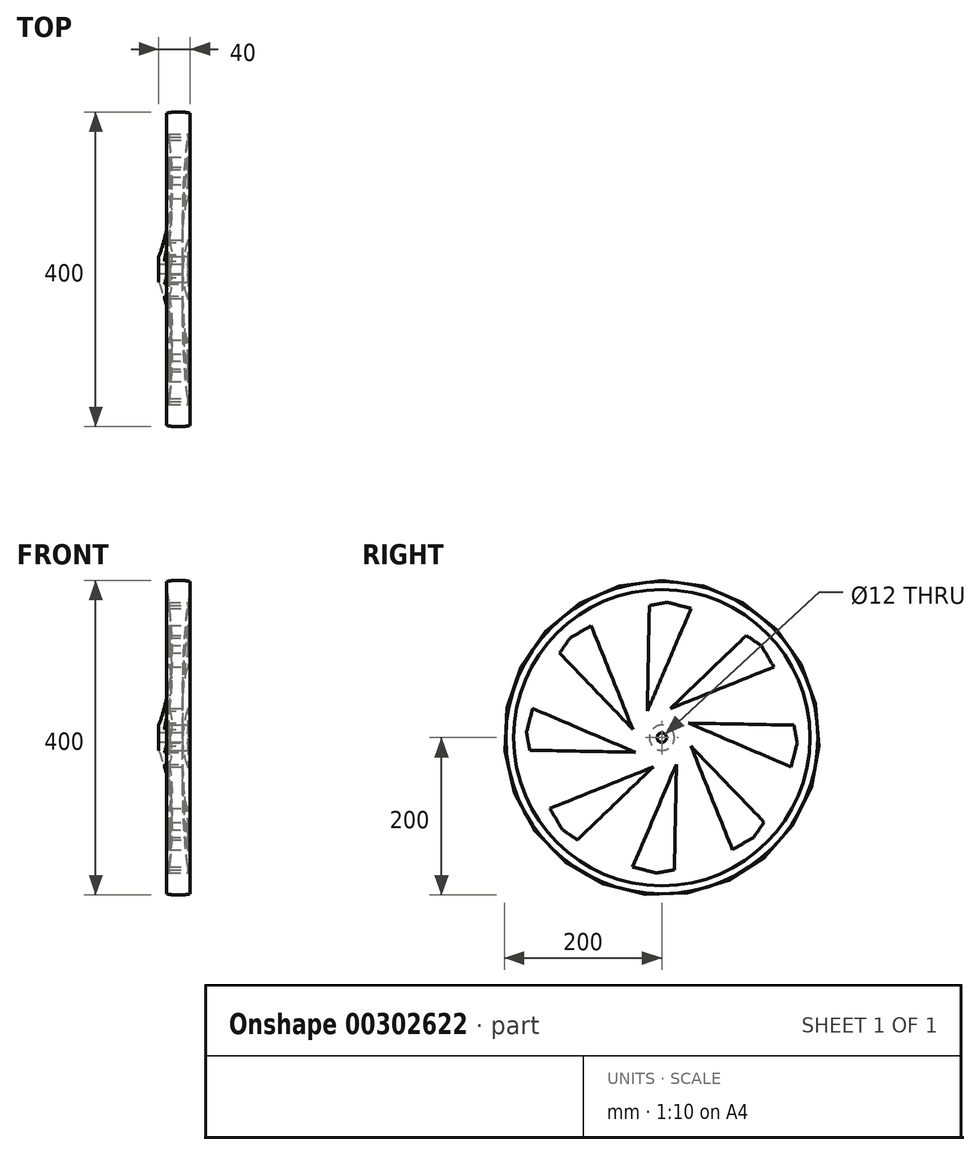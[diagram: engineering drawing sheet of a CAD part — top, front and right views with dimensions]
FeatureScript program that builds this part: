
annotation { "Feature Type Name" : "Feature", "Feature Type Description" : "" }
export const myFeature = defineFeature(function(context is Context, id is Id, definition is map)
    precondition{}
    {
        {
            var Q0;
            Q0=qCreatedBy(makeId("Front.planeOp"),FACE);
            var sketch = newSketch(context, id + "F0", { "sketchPlane" : qUnion([Q0])});
            skLineSegment(sketch, "E0", {"start": v(0, 0) * mm, "end": v(55.9, 0) * mm});
            skLineSegment(sketch, "E1", {"start": v(0, 0) * mm, "end": v(0, 200) * mm});
            skArc(sketch, "E2", {"start": v(15, 198.25) * mm, "mid": v(0, 200) * mm, "end": v(-15, 198.25) * mm});
            skLineSegment(sketch, "E3", {"start": v(-15, 198.25) * mm, "end": v(15, 198.25) * mm});
            skLineSegment(sketch, "E4", {"start": v(0, 0) * mm, "end": v(0, 6) * mm});
            skLineSegment(sketch, "E5", {"start": v(0, 6) * mm, "end": v(5, 6) * mm});
            skLineSegment(sketch, "E6", {"start": v(0, 6) * mm, "end": v(-25, 6) * mm});
            skLineSegment(sketch, "E7.top", {"start": v(-15, 188.25) * mm, "end": v(15, 188.25) * mm});
            skLineSegment(sketch, "E7.left", {"start": v(-15, 198.25) * mm, "end": v(-15, 188.25) * mm});
            skLineSegment(sketch, "E7.right", {"start": v(15, 198.25) * mm, "end": v(15, 188.25) * mm});
            skLineSegment(sketch, "E8.bottom", {"start": v(-25, 6) * mm, "end": v(5, 6) * mm});
            skLineSegment(sketch, "E8.top", {"start": v(-25, 16) * mm, "end": v(5, 16) * mm});
            skLineSegment(sketch, "E8.left", {"start": v(-25, 6) * mm, "end": v(-25, 16) * mm});
            skLineSegment(sketch, "E8.right", {"start": v(5, 6) * mm, "end": v(5, 16) * mm});
            skFitSpline(sketch, "E9", {"points": [v(15, 188.25) * mm, v(5, 16) * mm], "startDerivative": vector(-30, -169.88) * mm, "endDerivative": vector(0, -171.97) * mm});
            skFitSpline(sketch, "E10", {"points": [v(-15, 188.25) * mm, v(-25, 16) * mm], "startDerivative": vector(30, -169.88) * mm, "endDerivative": vector(-60, -162.6) * mm});
            skSolve(sketch);
        }
        {
            var Q0;
            Q0 = qSketchRegion(id + "F0", true);
            var Q1;
            Q1=sQuery(id+"F0.wireOp",EDGE,"E0");
            revolve(context, id + "F1", {"entities" : qUnion([Q0]), "axis" : qUnion([Q1]), "revolveType" : RevolveType.FULL});
        }
        {
            var Q0;
            Q0=makeQuery(id+"F1.opRevolve","SWEPT_FACE",FACE,{"disambiguationData":[OSD([sQuery(id+"F0.wireOp",EDGE,"E8.right")])]});
            var sketch = newSketch(context, id + "F2", { "sketchPlane" : qUnion([Q0])});
            skLineSegment(sketch, "E11", {"start": v(37.07, 164.14) * mm, "end": v(-18.52, 33.7) * mm});
            skLineSegment(sketch, "E12", {"start": v(-18.52, 33.7) * mm, "end": v(-15.93, 167.8) * mm});
            skLineSegment(sketch, "E13", {"start": v(-15.93, 167.8) * mm, "end": v(6.74, 171.99) * mm});
            skLineSegment(sketch, "E14", {"start": v(6.74, 171.99) * mm, "end": v(37.07, 164.14) * mm});
            skLineSegment(sketch, "E15.1.0", {"start": v(-116.85, 126.38) * mm, "end": v(-89.85, 142.28) * mm});
            skLineSegment(sketch, "E15.1.1", {"start": v(-129.91, 107.38) * mm, "end": v(-116.85, 126.38) * mm});
            skLineSegment(sketch, "E15.1.2", {"start": v(-89.85, 142.28) * mm, "end": v(-36.92, 10.73) * mm});
            skLineSegment(sketch, "E15.1.3", {"start": v(-36.92, 10.73) * mm, "end": v(-129.91, 107.38) * mm});
            skLineSegment(sketch, "E15.2.0", {"start": v(-171.99, 6.74) * mm, "end": v(-164.14, 37.07) * mm});
            skLineSegment(sketch, "E15.2.1", {"start": v(-167.8, -15.93) * mm, "end": v(-171.99, 6.74) * mm});
            skLineSegment(sketch, "E15.2.2", {"start": v(-164.14, 37.07) * mm, "end": v(-33.7, -18.52) * mm});
            skLineSegment(sketch, "E15.2.3", {"start": v(-33.7, -18.52) * mm, "end": v(-167.8, -15.93) * mm});
            skLineSegment(sketch, "E15.3.0", {"start": v(-126.38, -116.85) * mm, "end": v(-142.28, -89.85) * mm});
            skLineSegment(sketch, "E15.3.1", {"start": v(-107.38, -129.91) * mm, "end": v(-126.38, -116.85) * mm});
            skLineSegment(sketch, "E15.3.2", {"start": v(-142.28, -89.85) * mm, "end": v(-10.73, -36.92) * mm});
            skLineSegment(sketch, "E15.3.3", {"start": v(-10.73, -36.92) * mm, "end": v(-107.38, -129.91) * mm});
            skLineSegment(sketch, "E15.4.0", {"start": v(-6.74, -171.99) * mm, "end": v(-37.07, -164.14) * mm});
            skLineSegment(sketch, "E15.4.1", {"start": v(15.93, -167.8) * mm, "end": v(-6.74, -171.99) * mm});
            skLineSegment(sketch, "E15.4.2", {"start": v(-37.07, -164.14) * mm, "end": v(18.52, -33.7) * mm});
            skLineSegment(sketch, "E15.4.3", {"start": v(18.52, -33.7) * mm, "end": v(15.93, -167.8) * mm});
            skLineSegment(sketch, "E15.5.0", {"start": v(116.85, -126.38) * mm, "end": v(89.85, -142.28) * mm});
            skLineSegment(sketch, "E15.5.1", {"start": v(129.91, -107.38) * mm, "end": v(116.85, -126.38) * mm});
            skLineSegment(sketch, "E15.5.2", {"start": v(89.85, -142.28) * mm, "end": v(36.92, -10.73) * mm});
            skLineSegment(sketch, "E15.5.3", {"start": v(36.92, -10.73) * mm, "end": v(129.91, -107.38) * mm});
            skLineSegment(sketch, "E15.6.0", {"start": v(171.99, -6.74) * mm, "end": v(164.14, -37.07) * mm});
            skLineSegment(sketch, "E15.6.1", {"start": v(167.8, 15.93) * mm, "end": v(171.99, -6.74) * mm});
            skLineSegment(sketch, "E15.6.2", {"start": v(164.14, -37.07) * mm, "end": v(33.7, 18.52) * mm});
            skLineSegment(sketch, "E15.6.3", {"start": v(33.7, 18.52) * mm, "end": v(167.8, 15.93) * mm});
            skLineSegment(sketch, "E15.7.0", {"start": v(126.38, 116.85) * mm, "end": v(142.28, 89.85) * mm});
            skLineSegment(sketch, "E15.7.1", {"start": v(107.38, 129.91) * mm, "end": v(126.38, 116.85) * mm});
            skLineSegment(sketch, "E15.7.2", {"start": v(142.28, 89.85) * mm, "end": v(10.73, 36.92) * mm});
            skLineSegment(sketch, "E15.7.3", {"start": v(10.73, 36.92) * mm, "end": v(107.38, 129.91) * mm});
            skPoint(sketch, "E15.center", {"position": v(0, 0) * mm});
            skSolve(sketch);
        }
        {
            var Q0;
            Q0 = qSketchRegion(id + "F2", true);
            extrude(context, id + "F3", {"entities" : qUnion([Q0]), "operationType" : NewBodyOperationType.REMOVE, "endBound" : BoundingType.SYMMETRIC, "oppositeDirection" : true, "depth" : 60 * mm});
        }
    });
